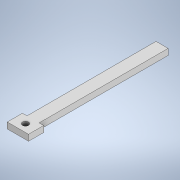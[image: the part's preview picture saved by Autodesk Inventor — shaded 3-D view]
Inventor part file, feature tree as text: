
AUTODESK INVENTOR PART (.ipt)
format: ipt  version: 2020 (Build 240168000, 168)  size: 123,392 bytes
history: native  units: mm
features: extrude x4, sketch x4
ambient origin geometry x8: Origin, YZ Plane, XZ Plane, XY Plane, X Axis, Y Axis, Z Axis, Center Point
bodies: Solid1 (feature_tree)
feature tree (8):
  extrude  "Extrusion1"  Depth=85.0mm
  extrude  "Extrusion2"  Depth=4.0mm
  extrude  "Extrusion3"  Depth=4.0mm TaperAngle=0.0deg
  extrude  "Extrusion4"  Depth=10.0mm
  sketch  "Sketch1"  dims[d0=8.0mm d1=85.0mm]
  sketch  "Sketch2"  dims[d2=4.0mm d3=0.0mm d4=7.0mm]
  sketch  "Sketch3"  dims[d5=10.0mm d6=4.0mm d7=0.0mm]
  sketch  "Sketch5"  dims[d8=7.0mm d9=10.0mm d10=4.0mm d11=0.0mm d14=7.0mm d15=5.0mm d16=4.0mm d17=4.0mm d18=0.0mm]
